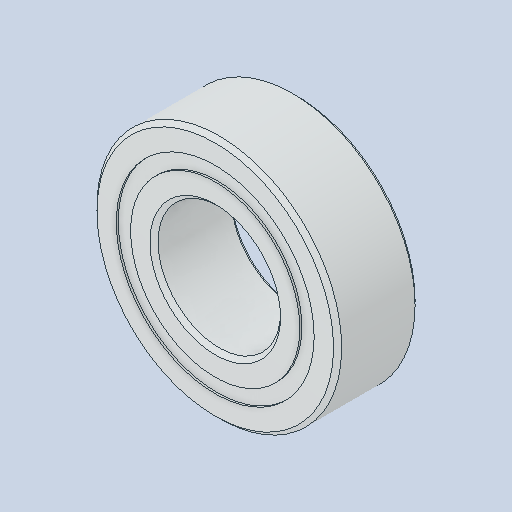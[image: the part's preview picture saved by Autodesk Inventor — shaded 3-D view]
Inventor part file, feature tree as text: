
AUTODESK INVENTOR PART (.ipt)
format: ipt  version: 2023.4 (Build 274418000, 418)  size: 587,776 bytes
history: native  units: in
note: dims shown in document units (in); Inventor stores cm internally (conversion verified against a paired STEP export)
features: other x11, revolve x5
ambient origin geometry x8: Origin, YZ Plane, XZ Plane, XY Plane, X Axis, Y Axis, Z Axis, Center Point
bodies: Solid1 (feature_tree), Solid2 (feature_tree), Solid3 (feature_tree), Solid4 (feature_tree), Solid5 (feature_tree), Solid6 (feature_tree), Solid7 (feature_tree), Solid8 (feature_tree), Solid9 (feature_tree), Solid10 (feature_tree), Solid11 (feature_tree), Solid12 (feature_tree), Solid13 (feature_tree), Solid14 (feature_tree), Solid15 (feature_tree), Solid16 (feature_tree)
feature tree (16):
  parser-record x1  (decoder bookkeeping rows leaked as tree rows — omitted from the tree; the rows remain in map.json)
  other  "CirPattern1[10]"
  revolve  "Revolve3"  [1 undecoded]
  other  "CirPattern1[2]"
  other  "CirPattern1[9]"
  other  "CirPattern1[4]"
  revolve  "Revolve4"  [1 undecoded]
  revolve  "Revolve5[1]"  [1 undecoded]
  other  "CirPattern1[1]"
  revolve  "Revolve1"  [1 undecoded]
  other  "CirPattern1[7]"
  other  "CirPattern1[11]"
  other  "CirPattern1[3]"
  revolve  "Revolve5[2]"  [1 undecoded]
  other  "CirPattern1[5]"
  other  "CirPattern1[8]"
note: 5 required parameter values undecoded (feature->parameter linkage not recoverable at this tier; creation-order binding heuristic only, values carry confidence <= 0.55)
